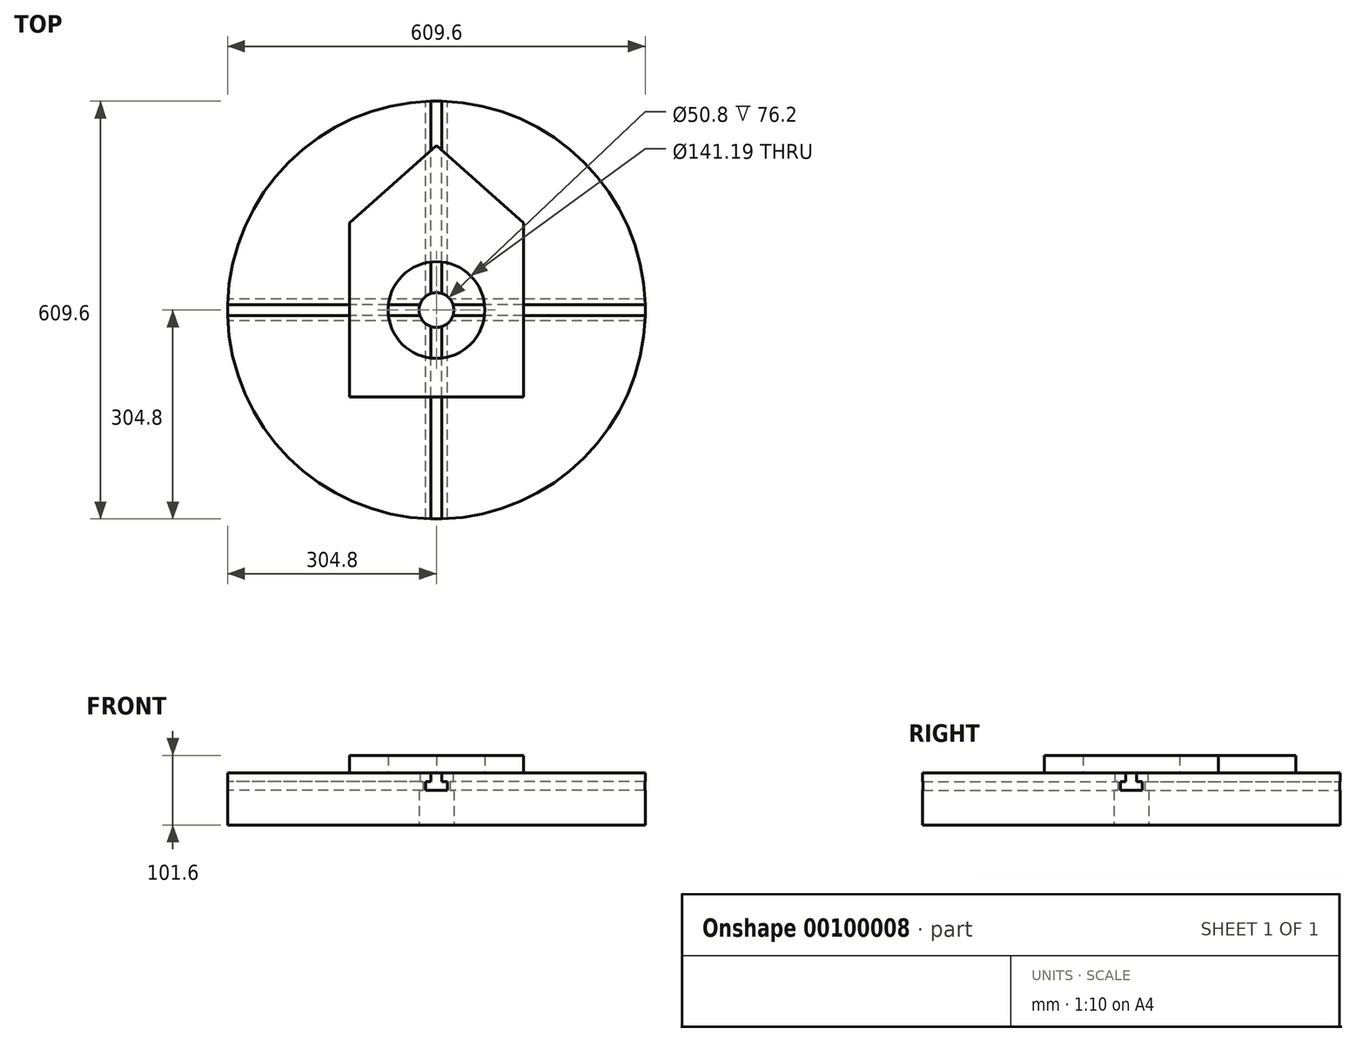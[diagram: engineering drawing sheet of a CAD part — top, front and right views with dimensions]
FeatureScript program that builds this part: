
annotation { "Feature Type Name" : "Feature", "Feature Type Description" : "" }
export const myFeature = defineFeature(function(context is Context, id is Id, definition is map)
    precondition{}
    {
        {
            var Q0;
            Q0=qCreatedBy(makeId("Top.planeOp"),FACE);
            var sketch = newSketch(context, id + "F0", { "sketchPlane" : qUnion([Q0])});
            skCircle(sketch, "E0", {"center": v(0, 0) * mm, "radius": 304.8 * mm});
            skCircle(sketch, "E1", {"center": v(0, 0) * mm, "radius": 25.4 * mm});
            skSolve(sketch);
        }
        {
            var Q0;
            Q0 = qSketchRegion(id + "F0", true);
            extrude(context, id + "F1", {"entities" : qUnion([Q0]), "depth" : 76.2 * mm});
        }
        {
            var Q0;
            Q0=qCreatedBy(makeId("Front.planeOp"),FACE);
            var sketch = newSketch(context, id + "F2", { "sketchPlane" : qUnion([Q0])});
            skLineSegment(sketch, "E2", {"start": v(-7.94, 76.2) * mm, "end": v(-7.94, 63.5) * mm});
            skLineSegment(sketch, "E3", {"start": v(-7.94, 63.5) * mm, "end": v(-15.88, 63.5) * mm});
            skLineSegment(sketch, "E4", {"start": v(-15.88, 63.5) * mm, "end": v(-15.88, 50.8) * mm});
            skLineSegment(sketch, "E5", {"start": v(-15.88, 50.8) * mm, "end": v(15.88, 50.8) * mm});
            skLineSegment(sketch, "E6", {"start": v(15.88, 50.8) * mm, "end": v(15.88, 63.5) * mm});
            skLineSegment(sketch, "E7", {"start": v(15.88, 63.5) * mm, "end": v(7.94, 63.5) * mm});
            skLineSegment(sketch, "E8", {"start": v(7.94, 63.5) * mm, "end": v(7.94, 76.2) * mm});
            skLineSegment(sketch, "E9", {"start": v(7.94, 76.2) * mm, "end": v(-7.94, 76.2) * mm});
            skLineSegment(sketch, "E10", {"start": v(0, 0) * mm, "end": v(0, 117.73) * mm, "construction": true});
            skSolve(sketch);
        }
        {
            var Q0;
            Q0=makeQuery(id+"F2.imprint","IMPRINT",FACE,{"disambiguationData":[TD([[makeQuery(id+"F2.imprint","IMPRINT",EDGE,{"derivedFrom":sQuery(id+"F2.wireOp",EDGE,"E2")}),1.0]])]});
            extrude(context, id + "F3", {"entities" : qUnion([Q0]), "endBound" : BoundingType.THROUGH_ALL, "depth" : 25.4 * mm, "hasSecondDirection" : true, "secondDirectionBound" : SecondDirectionBoundingType.THROUGH_ALL, "secondDirectionOppositeDirection" : true, "secondDirectionDepth" : 25.4 * mm});
        }
        {
            var Q0;
            Q0=makeQuery(id+"F3.opExtrude","SWEPT_BODY",BODY,{"disambiguationData":[OSD([sQuery(id+"F2.wireOp",EDGE,"E2"),sQuery(id+"F2.wireOp",EDGE,"E3"),sQuery(id+"F2.wireOp",EDGE,"E4"),sQuery(id+"F2.wireOp",EDGE,"E5"),sQuery(id+"F2.wireOp",EDGE,"E6"),sQuery(id+"F2.wireOp",EDGE,"E7"),sQuery(id+"F2.wireOp",EDGE,"E8"),sQuery(id+"F2.wireOp",EDGE,"E9")])]});
            var Q1;
            Q1=sQuery(id+"F2.wireOp",EDGE,"E10");
            circularPattern(context, id + "F4", {"entities" : qUnion([Q0]), "axis" : qUnion([Q1]), "angle" : 90 * degree, "instanceCount" : 2});
        }
        {
            var Q0;
            Q0=makeQuery(id+"F4.opPattern","COPY",BODY,{"derivedFrom":makeQuery(id+"F3.opExtrude","SWEPT_BODY",BODY,{"disambiguationData":[OSD([sQuery(id+"F2.wireOp",EDGE,"E2"),sQuery(id+"F2.wireOp",EDGE,"E3"),sQuery(id+"F2.wireOp",EDGE,"E4"),sQuery(id+"F2.wireOp",EDGE,"E5"),sQuery(id+"F2.wireOp",EDGE,"E6"),sQuery(id+"F2.wireOp",EDGE,"E7"),sQuery(id+"F2.wireOp",EDGE,"E8"),sQuery(id+"F2.wireOp",EDGE,"E9")])]}),"instanceName":"1"});
            var Q1;
            Q1=makeQuery(id+"F3.opExtrude","SWEPT_BODY",BODY,{"disambiguationData":[OSD([sQuery(id+"F2.wireOp",EDGE,"E2"),sQuery(id+"F2.wireOp",EDGE,"E3"),sQuery(id+"F2.wireOp",EDGE,"E4"),sQuery(id+"F2.wireOp",EDGE,"E5"),sQuery(id+"F2.wireOp",EDGE,"E6"),sQuery(id+"F2.wireOp",EDGE,"E7"),sQuery(id+"F2.wireOp",EDGE,"E8"),sQuery(id+"F2.wireOp",EDGE,"E9")])]});
            var Q2;
            Q2=makeQuery(id+"F4.opPattern","COPY",BODY,{"derivedFrom":makeQuery(id+"F3.opExtrude","SWEPT_BODY",BODY,{"disambiguationData":[OSD([sQuery(id+"F2.wireOp",EDGE,"E2"),sQuery(id+"F2.wireOp",EDGE,"E3"),sQuery(id+"F2.wireOp",EDGE,"E4"),sQuery(id+"F2.wireOp",EDGE,"E5"),sQuery(id+"F2.wireOp",EDGE,"E6"),sQuery(id+"F2.wireOp",EDGE,"E7"),sQuery(id+"F2.wireOp",EDGE,"E8"),sQuery(id+"F2.wireOp",EDGE,"E9")])]}),"instanceName":"2"});
            var Q3;
            Q3=makeQuery(id+"F1.opExtrude","SWEPT_BODY",BODY,{"disambiguationData":[OSD([sQuery(id+"F0.wireOp",EDGE,"E0"),sQuery(id+"F0.wireOp",EDGE,"E1")])]});
            booleanBodies(context, id + "F5", {"operationType" : BooleanOperationType.SUBTRACTION, "tools" : qUnion([Q0, Q1, Q2]), "targets" : qUnion([Q3])});
        }
        {
            var Q0;
            {var subQ0=sQuery(id+"F0.wireOp",EDGE,"E0");var subQ1=sQuery(id+"F0.wireOp",EDGE,"E1");Q0=makeQuery(id+"F5.opBoolean","SPLIT",FACE,{"disambiguationData":[TD([makeQuery(id+"F1.opExtrude","SWEPT_FACE",FACE,{"disambiguationData":[OSD([subQ0])]}),makeQuery(id+"F1.opExtrude","SWEPT_FACE",FACE,{"disambiguationData":[OSD([subQ1])]}),makeQuery(id+"F3.opExtrude","SWEPT_FACE",FACE,{"disambiguationData":[OSD([sQuery(id+"F2.wireOp",EDGE,"E2")])]}),makeQuery(id+"F4.opPattern","COPY",FACE,{"derivedFrom":makeQuery(id+"F3.opExtrude","SWEPT_FACE",FACE,{"disambiguationData":[OSD([sQuery(id+"F2.wireOp",EDGE,"E8")])]}),"instanceName":"1"})])],"derivedFrom":makeQuery(id+"F1.opExtrude","CAP_FACE",FACE,{"disambiguationData":[OSD([subQ0,subQ1])],"isStart":false})});}
            var sketch = newSketch(context, id + "F6", { "sketchPlane" : qUnion([Q0])});
            skLineSegment(sketch, "E11.bottom", {"start": v(-127, 127) * mm, "end": v(127, 127) * mm});
            skLineSegment(sketch, "E11.top", {"start": v(-127, -127) * mm, "end": v(127, -127) * mm});
            skLineSegment(sketch, "E11.left", {"start": v(-127, 127) * mm, "end": v(-127, -127) * mm});
            skLineSegment(sketch, "E11.right", {"start": v(127, 127) * mm, "end": v(127, -127) * mm});
            skPoint(sketch, "E11.middle", {"position": v(0, 0) * mm});
            skLineSegment(sketch, "E12", {"start": v(-127, 127) * mm, "end": v(0, 240.08) * mm});
            skLineSegment(sketch, "E13", {"start": v(0, 240.08) * mm, "end": v(127, 127) * mm});
            skCircle(sketch, "E14", {"center": v(0, 0) * mm, "radius": 70.6 * mm});
            skSolve(sketch);
        }
        {
            var Q0;
            {var subQ1=sQuery(id+"F6.wireOp",EDGE,"E11.top");Q0=makeQuery(id+"F6.imprint","IMPRINT",FACE,{"disambiguationData":[TD([[makeQuery(id+"F6.imprint","IMPRINT",EDGE,{"derivedFrom":subQ1}),1.0]])]});}
            var Q1;
            {var subQ0=sQuery(id+"F6.wireOp",EDGE,"E11.left");var subQ8=sQuery(id+"F6.wireOp",EDGE,"E11.bottom");var subQ9=makeQuery(id+"F6.imprint","INTERSECT",VERTEX,{"derivedFrom":[subQ8,subQ0,sQuery(id+"F6.wireOp",EDGE,"E12")]});Q1=makeQuery(id+"F6.imprint","IMPRINT",FACE,{"disambiguationData":[TD([[makeQuery(id+"F6.imprint","IMPRINT",EDGE,{"disambiguationData":[TD([[subQ9,-1.0]])],"derivedFrom":subQ8}),-1.0]])]});}
            var Q2;
            {var subQ0=sQuery(id+"F6.wireOp",EDGE,"E12");var subQ1=sQuery(id+"F6.wireOp",EDGE,"E11.bottom");var subQ2=makeQuery(id+"F6.imprint","INTERSECT",VERTEX,{"derivedFrom":[subQ1,sQuery(id+"F6.wireOp",EDGE,"E11.left"),subQ0]});Q2=makeQuery(id+"F6.imprint","IMPRINT",FACE,{"disambiguationData":[TD([[makeQuery(id+"F6.imprint","IMPRINT",EDGE,{"disambiguationData":[TD([[subQ2,-1.0]])],"derivedFrom":subQ1}),1.0]])]});}
            var Q3;
            {var subQ0=sQuery(id+"F6.wireOp",EDGE,"E13");Q3=makeQuery(id+"F6.imprint","IMPRINT",FACE,{"disambiguationData":[TD([[makeQuery(id+"F6.imprint","IMPRINT",EDGE,{"derivedFrom":subQ0}),-1.0]])]});}
            extrude(context, id + "F7", {"entities" : qUnion([Q0, Q1, Q2, Q3]), "depth" : 25.4 * mm});
        }
    });
